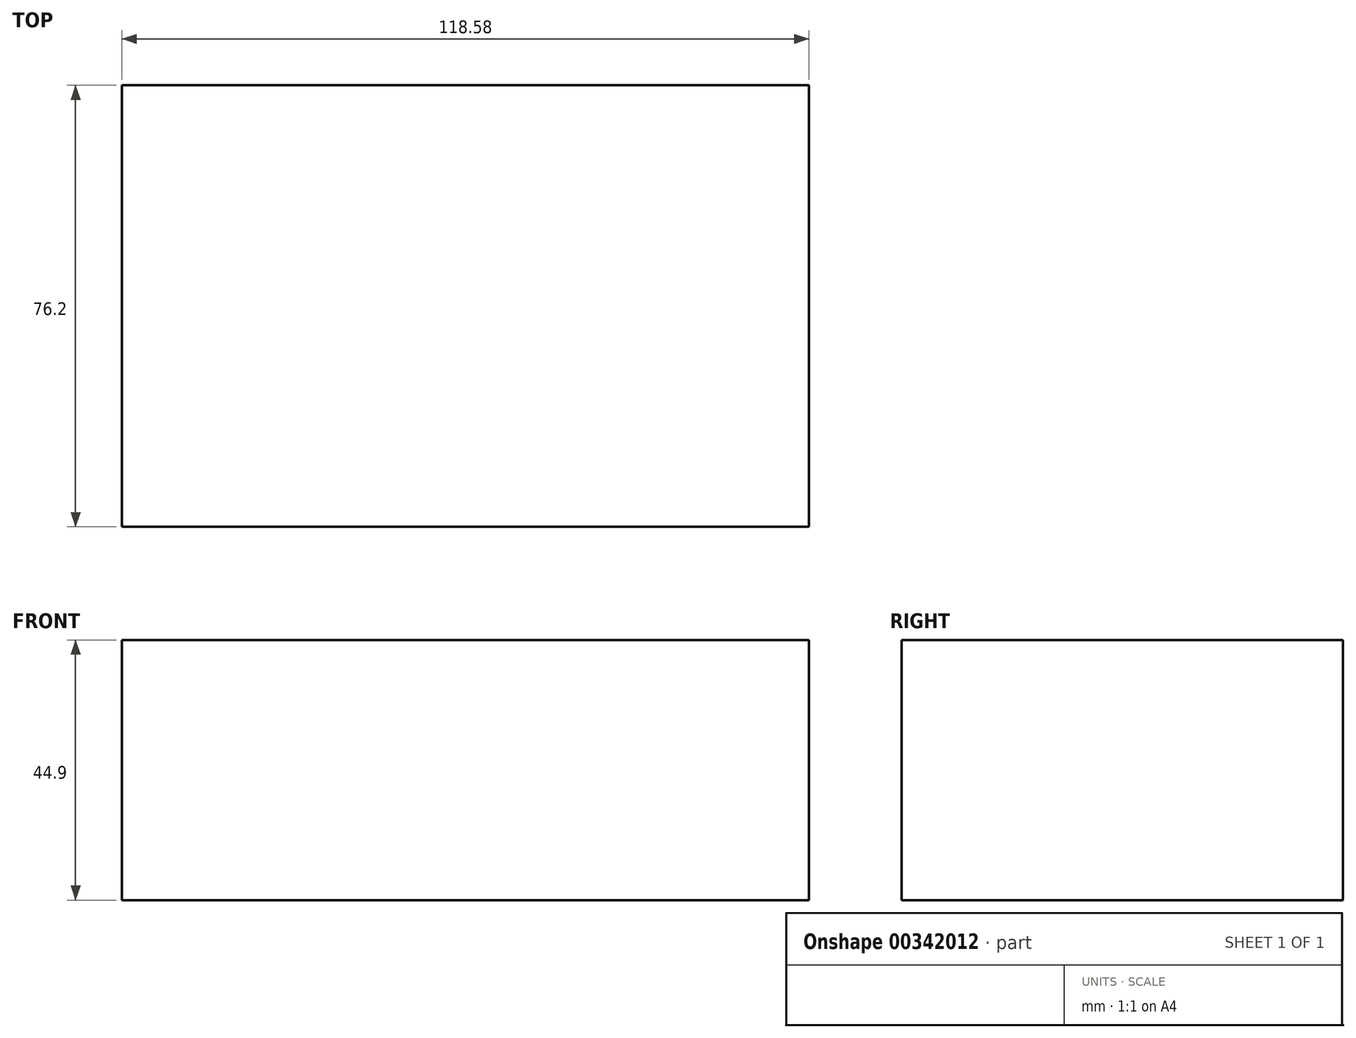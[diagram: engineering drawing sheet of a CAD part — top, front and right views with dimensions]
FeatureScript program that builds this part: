
annotation { "Feature Type Name" : "Feature", "Feature Type Description" : "" }
export const myFeature = defineFeature(function(context is Context, id is Id, definition is map)
    precondition{}
    {
        {
            var Q0;
            Q0=qCreatedBy(makeId("Front.planeOp"),FACE);
            var sketch = newSketch(context, id + "F0", { "sketchPlane" : qUnion([Q0])});
            skLineSegment(sketch, "E0.bottom", {"start": v(59.29, -22.45) * mm, "end": v(-59.29, -22.45) * mm});
            skLineSegment(sketch, "E0.top", {"start": v(59.29, 22.45) * mm, "end": v(-59.29, 22.45) * mm});
            skLineSegment(sketch, "E0.left", {"start": v(59.29, -22.45) * mm, "end": v(59.29, 22.45) * mm});
            skLineSegment(sketch, "E0.right", {"start": v(-59.29, -22.45) * mm, "end": v(-59.29, 22.45) * mm});
            skPoint(sketch, "E0.middle", {"position": v(0, 0) * mm});
            skCircle(sketch, "E1", {"center": v(71.14, 62.71) * mm, "radius": 28.85 * mm});
            skFitSpline(sketch, "E2", {"points": [v(-59.29, 22.45) * mm, v(50.74, 83.12) * mm], "startDerivative": vector(129.3, 19.2) * mm, "endDerivative": vector(152.23, 16.53) * mm});
            skLineSegment(sketch, "E3", {"start": v(59.29, 22.45) * mm, "end": v(59.29, 36.41) * mm});
            skSolve(sketch);
        }
        {
            var Q0;
            Q0=makeQuery(id+"F0.imprint","IMPRINT",FACE,{"disambiguationData":[TD([[makeQuery(id+"F0.imprint","IMPRINT",EDGE,{"derivedFrom":sQuery(id+"F0.wireOp",EDGE,"E0.bottom")}),-1.0]])]});
            extrude(context, id + "F1", {"entities" : qUnion([Q0]), "endBound" : BoundingType.SYMMETRIC, "depth" : 76.2 * mm});
        }
    });
